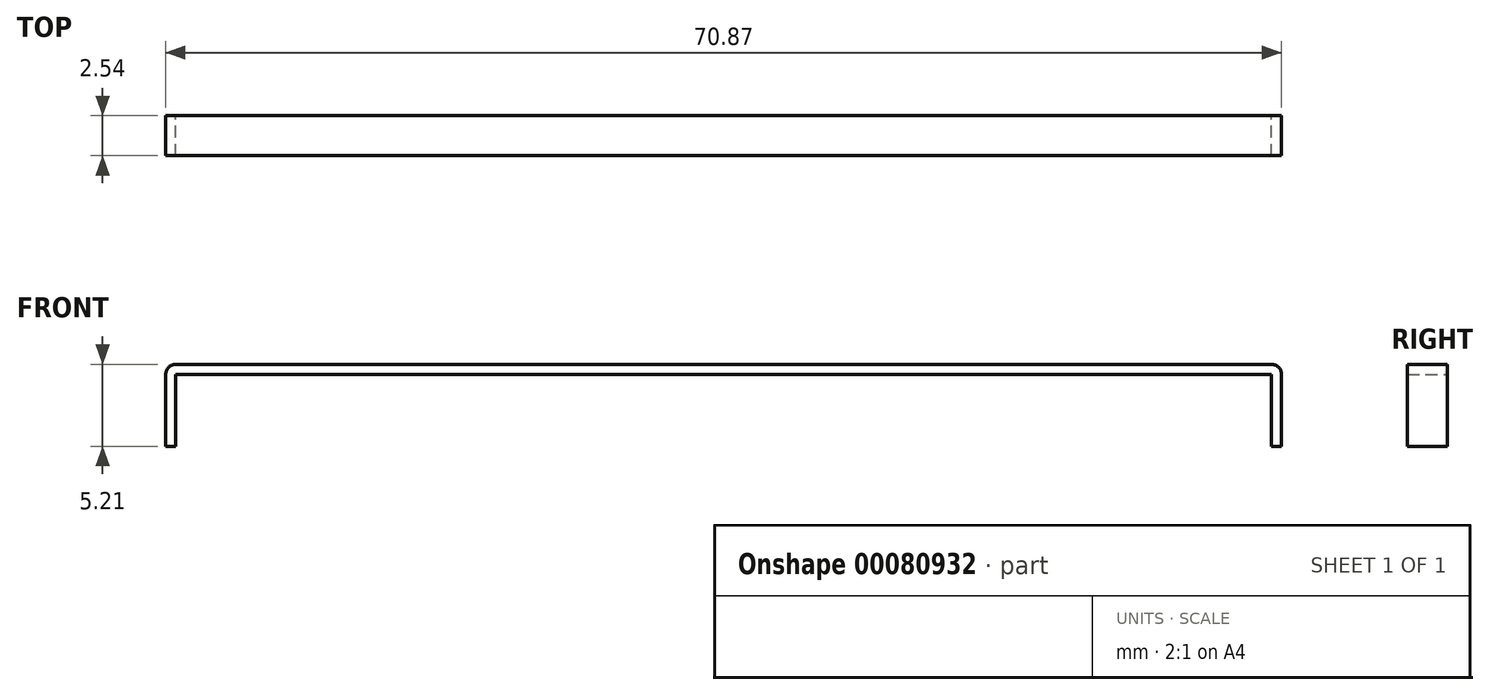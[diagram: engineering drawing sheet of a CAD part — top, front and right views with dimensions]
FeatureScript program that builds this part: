
annotation { "Feature Type Name" : "Feature", "Feature Type Description" : "" }
export const myFeature = defineFeature(function(context is Context, id is Id, definition is map)
    precondition{}
    {
        {
            var Q0;
            Q0=qCreatedBy(makeId("Front.planeOp"),FACE);
            var sketch = newSketch(context, id + "F0", { "sketchPlane" : qUnion([Q0])});
            skLineSegment(sketch, "E0", {"start": v(0, 0) * mm, "end": v(69.6, 0) * mm});
            skLineSegment(sketch, "E1", {"start": v(69.6, 0) * mm, "end": v(69.6, -4.57) * mm});
            skLineSegment(sketch, "E2", {"start": v(69.6, -4.57) * mm, "end": v(70.23, -4.57) * mm});
            skLineSegment(sketch, "E3", {"start": v(70.23, -4.57) * mm, "end": v(70.23, 0) * mm});
            skLineSegment(sketch, "E4", {"start": v(69.6, 0.64) * mm, "end": v(0, 0.63) * mm});
            skLineSegment(sketch, "E5", {"start": v(-0.64, 0) * mm, "end": v(-0.64, -4.57) * mm});
            skLineSegment(sketch, "E6", {"start": v(-0.64, -4.57) * mm, "end": v(0, -4.57) * mm});
            skLineSegment(sketch, "E7", {"start": v(0, -4.57) * mm, "end": v(0, 0) * mm});
            skPoint(sketch, "E8.visualSharp", {"position": v(-0.64, 0.63) * mm});
            skArc(sketch, "E8.filletArc", {"start": v(0, 0.63) * mm, "mid": v(-0.45, 0.45) * mm, "end": v(-0.64, 0) * mm});
            skPoint(sketch, "E9.visualSharp", {"position": v(70.23, 0.64) * mm});
            skArc(sketch, "E9.filletArc", {"start": v(70.23, 0) * mm, "mid": v(70.05, 0.45) * mm, "end": v(69.6, 0.64) * mm});
            skSolve(sketch);
        }
        {
            var Q0;
            Q0=makeQuery(id+"F0.imprint","IMPRINT",FACE,{"disambiguationData":[TD([[makeQuery(id+"F0.imprint","IMPRINT",EDGE,{"derivedFrom":sQuery(id+"F0.wireOp",EDGE,"E0")}),1.0]])]});
            extrude(context, id + "F1", {"entities" : qUnion([Q0]), "depth" : 2.54 * mm, "symmetric" : true});
        }
    });
